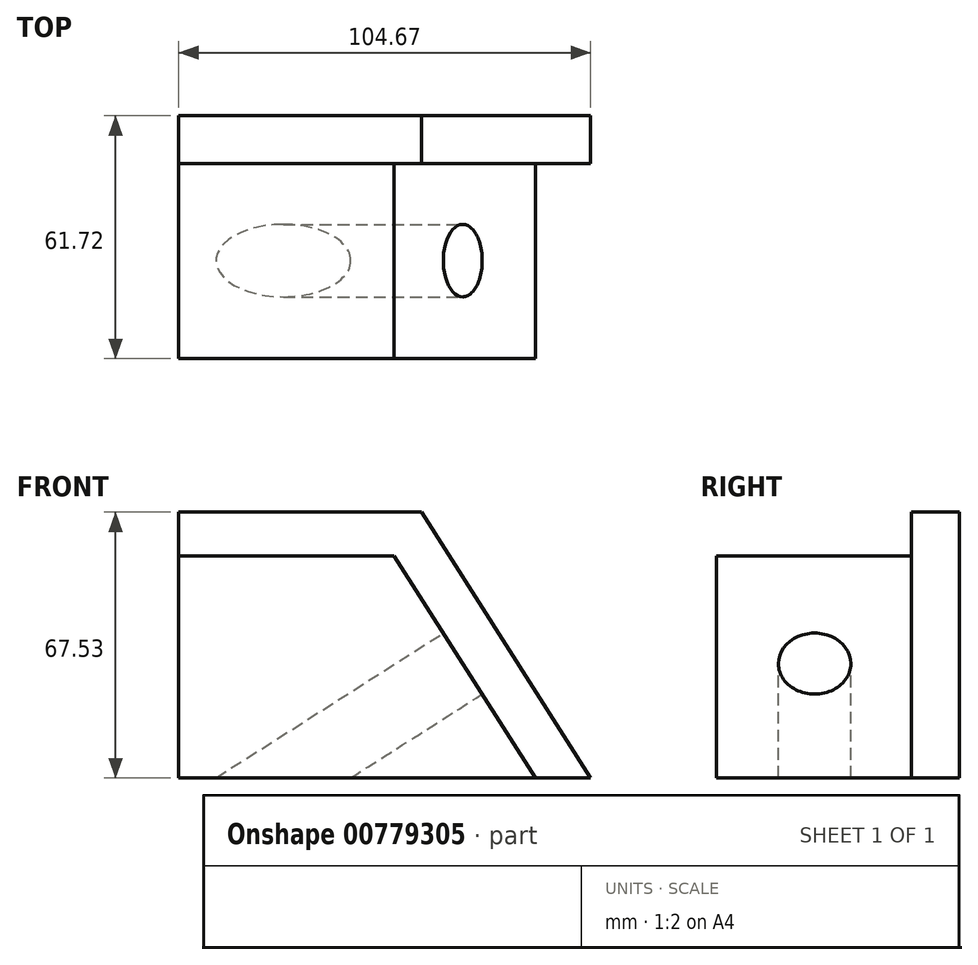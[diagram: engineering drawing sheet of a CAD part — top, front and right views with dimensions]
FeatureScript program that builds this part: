
annotation { "Feature Type Name" : "Feature", "Feature Type Description" : "" }
export const myFeature = defineFeature(function(context is Context, id is Id, definition is map)
    precondition{}
    {
        {
            var Q0;
            Q0=qCreatedBy(makeId("Front.planeOp"),FACE);
            var sketch = newSketch(context, id + "F0", { "sketchPlane" : qUnion([Q0])});
            skLineSegment(sketch, "E0.bottom", {"start": v(-76.25, 67.53) * mm, "end": v(-14.59, 67.53) * mm});
            skLineSegment(sketch, "E0.top", {"start": v(-76.25, 0) * mm, "end": v(-14.59, 0) * mm});
            skLineSegment(sketch, "E0.left", {"start": v(-76.25, 67.53) * mm, "end": v(-76.25, 0) * mm});
            skLineSegment(sketch, "E1", {"start": v(-14.59, 67.53) * mm, "end": v(28.42, 0) * mm});
            skLineSegment(sketch, "E2", {"start": v(28.42, 0) * mm, "end": v(-14.59, 0) * mm});
            skLineSegment(sketch, "E3.bottom", {"start": v(-76.25, 56.4) * mm, "end": v(-21.5, 56.4) * mm});
            skLineSegment(sketch, "E3.top", {"start": v(-76.25, 0) * mm, "end": v(-21.5, 0) * mm});
            skLineSegment(sketch, "E3.left", {"start": v(-76.25, 56.4) * mm, "end": v(-76.25, 0) * mm});
            skLineSegment(sketch, "E4", {"start": v(-21.5, 56.4) * mm, "end": v(14.42, 0) * mm});
            skLineSegment(sketch, "E5", {"start": v(14.42, 0) * mm, "end": v(-21.5, 0) * mm});
            skSolve(sketch);
        }
        {
            var Q0;
            Q0=makeQuery(id+"F0.imprint","IMPRINT",FACE,{"disambiguationData":[TD([[makeQuery(id+"F0.imprint","IMPRINT",EDGE,{"derivedFrom":sQuery(id+"F0.wireOp",EDGE,"E3.bottom")}),-1.0]])]});
            extrude(context, id + "F1", {"entities" : qUnion([Q0]), "depth" : 61.72 * mm, "offsetDistance" : 25.4 * mm});
        }
        {
            var Q0;
            Q0 = qSketchRegion(id + "F0", true);
            extrude(context, id + "F2", {"entities" : qUnion([Q0]), "operationType" : NewBodyOperationType.ADD, "depth" : 12.2 * mm, "offsetDistance" : 25.4 * mm});
        }
        {
            var Q0;
            Q0=makeQuery(id+"F1.opExtrude","SWEPT_FACE",FACE,{"disambiguationData":[OSD([sQuery(id+"F0.wireOp",EDGE,"E4")])]});
            var sketch = newSketch(context, id + "F3", { "sketchPlane" : qUnion([Q0])});
            skCircle(sketch, "E6", {"center": v(-36.82, 26.67) * mm, "radius": 9.2 * mm});
            skSolve(sketch);
        }
        {
            var Q0;
            Q0=makeQuery(id+"F3.imprint","IMPRINT",FACE,{"disambiguationData":[TD([[makeQuery(id+"F3.imprint","IMPRINT",EDGE,{"derivedFrom":sQuery(id+"F3.wireOp",EDGE,"E6")}),1.0]])]});
            extrude(context, id + "F4", {"entities" : qUnion([Q0]), "operationType" : NewBodyOperationType.REMOVE, "endBound" : BoundingType.THROUGH_ALL, "oppositeDirection" : true, "depth" : 25.4 * mm, "offsetDistance" : 25.4 * mm});
        }
    });
